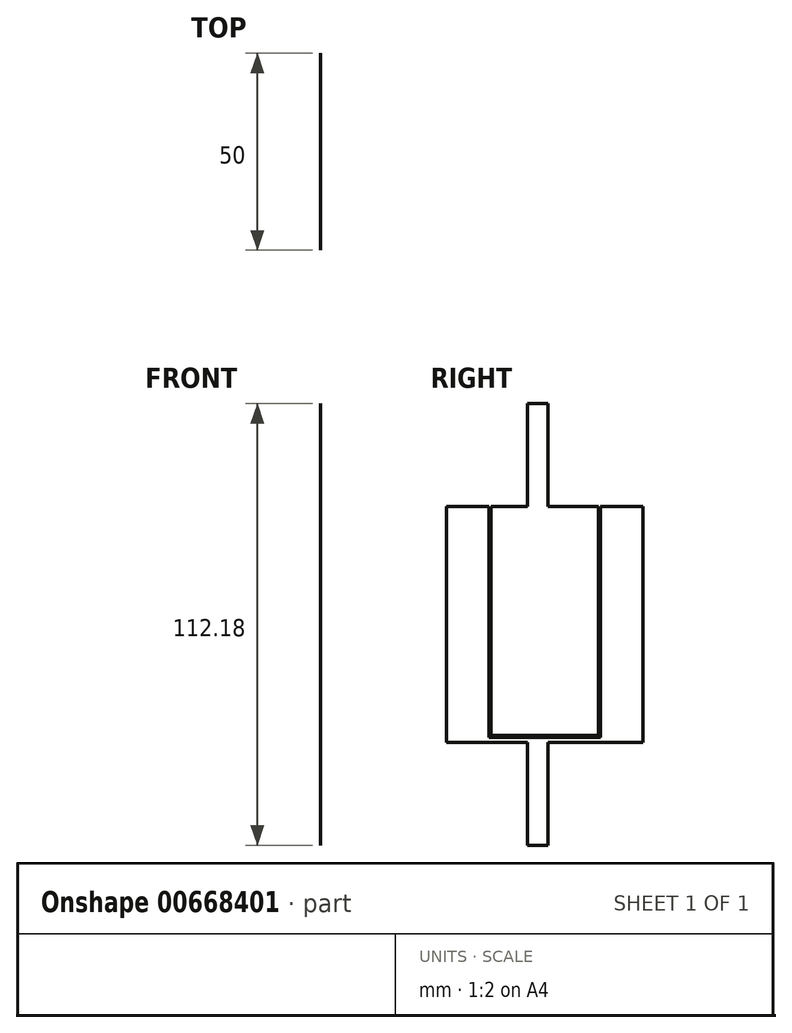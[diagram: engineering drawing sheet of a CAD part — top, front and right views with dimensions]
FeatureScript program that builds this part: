
annotation { "Feature Type Name" : "Feature", "Feature Type Description" : "" }
export const myFeature = defineFeature(function(context is Context, id is Id, definition is map)
    precondition{}
    {
        {
            var Q0;
            Q0=qCreatedBy(makeId("Right.planeOp"),FACE);
            var sketch = newSketch(context, id + "F0", { "sketchPlane" : qUnion([Q0])});
            skLineSegment(sketch, "E0", {"start": v(0, 0) * mm, "end": v(6.52, 0) * mm});
            skLineSegment(sketch, "E1", {"start": v(0, 0) * mm, "end": v(0, -60) * mm});
            skLineSegment(sketch, "E2", {"start": v(0, -60) * mm, "end": v(12.4, -60) * mm});
            skLineSegment(sketch, "E3", {"start": v(50, -60) * mm, "end": v(50, 0) * mm});
            skLineSegment(sketch, "E4", {"start": v(50, 0) * mm, "end": v(39.13, 0) * mm});
            skLineSegment(sketch, "E5.0", {"start": v(25.87, -60) * mm, "end": v(25.87, -81.07) * mm});
            skLineSegment(sketch, "E6", {"start": v(11.45, 0) * mm, "end": v(20.65, 0) * mm});
            skLineSegment(sketch, "E7.0", {"start": v(25.87, 0) * mm, "end": v(25.87, 26.09) * mm});
            skLineSegment(sketch, "E8.0", {"start": v(20.65, 0) * mm, "end": v(20.65, 26.09) * mm});
            skLineSegment(sketch, "E9", {"start": v(20.65, 26.09) * mm, "end": v(25.87, 26.09) * mm});
            skLineSegment(sketch, "E10", {"start": v(12, -60) * mm, "end": v(12.4, -60) * mm});
            skLineSegment(sketch, "E11", {"start": v(0, -60) * mm, "end": v(12, -60) * mm});
            skLineSegment(sketch, "E12", {"start": v(20.65, -86.09) * mm, "end": v(20.65, -60) * mm});
            skLineSegment(sketch, "E13.trimOffspring", {"start": v(25.87, -60) * mm, "end": v(50, -60) * mm});
            skPoint(sketch, "E14.trimOffspring.start.orphan", {"position": v(25, -60) * mm});
            skLineSegment(sketch, "E15", {"start": v(25.87, -81.07) * mm, "end": v(25.87, -86.09) * mm});
            skLineSegment(sketch, "E16", {"start": v(20.65, -86.09) * mm, "end": v(25.87, -86.09) * mm});
            skLineSegment(sketch, "E17", {"start": v(16.08, 0) * mm, "end": v(20.65, 0) * mm});
            skLineSegment(sketch, "E18.trimOffspring", {"start": v(25.87, 0) * mm, "end": v(38.63, 0) * mm});
            skLineSegment(sketch, "E19.trimOffspring", {"start": v(20.65, 0) * mm, "end": v(11.37, 0) * mm});
            skLineSegment(sketch, "E20.0", {"start": v(11.37, 0) * mm, "end": v(11.37, -26.74) * mm});
            skLineSegment(sketch, "E21.0", {"start": v(10.87, 0) * mm, "end": v(10.87, -27.64) * mm});
            skLineSegment(sketch, "E22.0", {"start": v(39.13, -27.64) * mm, "end": v(39.13, 0) * mm});
            skLineSegment(sketch, "E23.0", {"start": v(38.63, -26.74) * mm, "end": v(38.63, 0) * mm});
            skLineSegment(sketch, "E24", {"start": v(11.37, -27.14) * mm, "end": v(11.37, -26.74) * mm});
            skLineSegment(sketch, "E25", {"start": v(11.37, 0) * mm, "end": v(16.08, 0) * mm});
            skLineSegment(sketch, "E26", {"start": v(10.87, 0) * mm, "end": v(6.52, 0) * mm});
            skLineSegment(sketch, "E27", {"start": v(38.63, -27.14) * mm, "end": v(38.63, -26.74) * mm});
            skLineSegment(sketch, "E28.0", {"start": v(10.87, -58.7) * mm, "end": v(39.13, -58.7) * mm});
            skLineSegment(sketch, "E29", {"start": v(10.87, -27.64) * mm, "end": v(10.87, -58.7) * mm});
            skLineSegment(sketch, "E30", {"start": v(39.13, -27.64) * mm, "end": v(39.13, -58.7) * mm});
            skLineSegment(sketch, "E31", {"start": v(38.63, -27.14) * mm, "end": v(38.63, -58.2) * mm});
            skLineSegment(sketch, "E32", {"start": v(11.37, -27.14) * mm, "end": v(11.37, -58.2) * mm});
            skLineSegment(sketch, "E33.0", {"start": v(11.37, -58.2) * mm, "end": v(38.63, -58.2) * mm});
            skLineSegment(sketch, "E34", {"start": v(0, -60) * mm, "end": v(20.65, -60) * mm});
            skLineSegment(sketch, "E35.trimOffspring", {"start": v(20.65, -60) * mm, "end": v(0, -60) * mm});
            skLineSegment(sketch, "E36.trimOffspring", {"start": v(10.87, 0) * mm, "end": v(9, 0) * mm});
            skLineSegment(sketch, "E37.trimOffspring", {"start": v(39.13, 0) * mm, "end": v(50, 0) * mm});
            skLineSegment(sketch, "E38.trimOffspring", {"start": v(38.63, 0) * mm, "end": v(25.87, 0) * mm});
            skSolve(sketch);
        }
        {
            var Q0;
            Q0=makeQuery(id+"F0.imprint","IMPRINT",FACE,{"disambiguationData":[TD([[makeQuery(id+"F0.imprint","IMPRINT",EDGE,{"derivedFrom":sQuery(id+"F0.wireOp",EDGE,"b56e8115-747c-47a9-926b-84bb7afac1cf.0")}),1.0]])]});
            var Q1;
            Q1=makeQuery(id+"F0.imprint","IMPRINT",FACE,{"disambiguationData":[TD([[makeQuery(id+"F0.imprint","IMPRINT",EDGE,{"derivedFrom":sQuery(id+"F0.wireOp",EDGE,"E0")}),-1.0]])]});
            var Q2;
            Q2=makeQuery(id+"F0.imprint","IMPRINT",FACE,{"disambiguationData":[TD([[makeQuery(id+"F0.imprint","IMPRINT",EDGE,{"derivedFrom":sQuery(id+"F0.wireOp",EDGE,"8dee40f3-ee80-49ba-9f93-c100ff8cb728.0")}),1.0]])]});
            var Q3;
            Q3=makeQuery(id+"F0.imprint","IMPRINT",FACE,{"disambiguationData":[TD([[makeQuery(id+"F0.imprint","IMPRINT",EDGE,{"derivedFrom":sQuery(id+"F0.wireOp",EDGE,"E7.0")}),1.0]])]});
            extrude(context, id + "F1", {"entities" : qUnion([Q0, Q1, Q2, Q3]), "depth" : 0 * mm, "offsetDistance" : 25 * mm});
        }
    });
